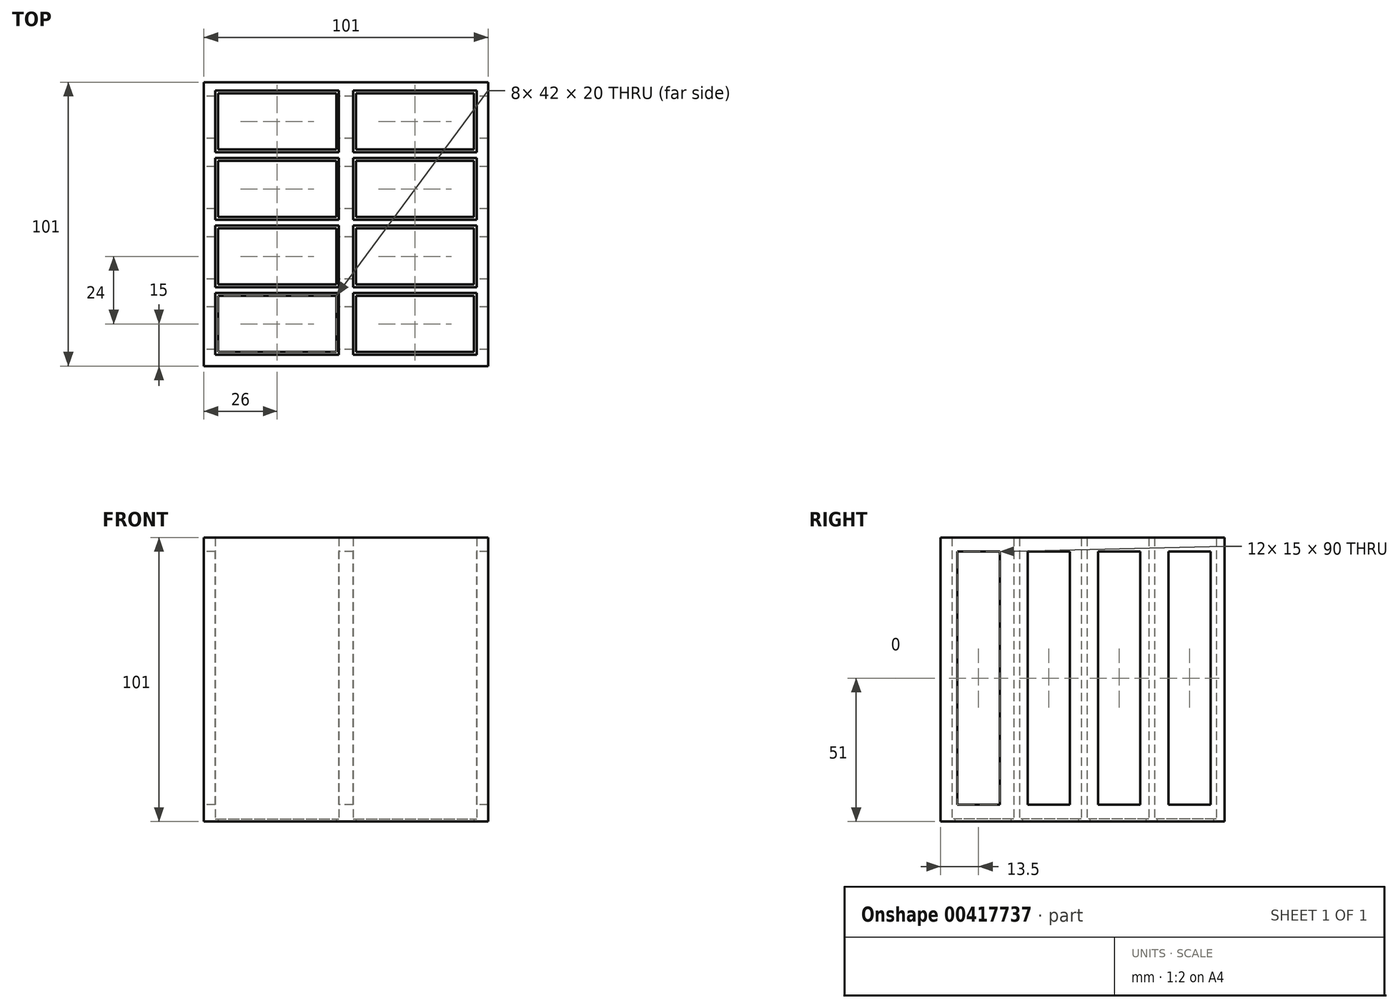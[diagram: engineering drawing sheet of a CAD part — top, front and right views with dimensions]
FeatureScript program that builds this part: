
annotation { "Feature Type Name" : "Feature", "Feature Type Description" : "" }
export const myFeature = defineFeature(function(context is Context, id is Id, definition is map)
    precondition{}
    {
        {
            var Q0;
            Q0=qCreatedBy(makeId("Top.planeOp"),FACE);
            var sketch = newSketch(context, id + "F0", { "sketchPlane" : qUnion([Q0])});
            skLineSegment(sketch, "E0.bottom", {"start": v(0, 0) * mm, "end": v(101, 0) * mm});
            skLineSegment(sketch, "E0.top", {"start": v(0, 101) * mm, "end": v(101, 101) * mm});
            skLineSegment(sketch, "E0.left", {"start": v(0, 0) * mm, "end": v(0, 101) * mm});
            skLineSegment(sketch, "E0.right", {"start": v(101, 0) * mm, "end": v(101, 101) * mm});
            skLineSegment(sketch, "E1.bottom", {"start": v(5, 97) * mm, "end": v(47, 97) * mm});
            skLineSegment(sketch, "E1.top", {"start": v(5, 77) * mm, "end": v(47, 77) * mm});
            skLineSegment(sketch, "E1.left", {"start": v(5, 97) * mm, "end": v(5, 77) * mm});
            skLineSegment(sketch, "E1.right", {"start": v(47, 97) * mm, "end": v(47, 77) * mm});
            skLineSegment(sketch, "E2.0.1.0", {"start": v(5, 73) * mm, "end": v(47, 73) * mm});
            skLineSegment(sketch, "E2.0.1.1", {"start": v(5, 73) * mm, "end": v(5, 53) * mm});
            skLineSegment(sketch, "E2.0.1.2", {"start": v(5, 53) * mm, "end": v(47, 53) * mm});
            skLineSegment(sketch, "E2.0.1.3", {"start": v(47, 73) * mm, "end": v(47, 53) * mm});
            skLineSegment(sketch, "E2.0.2.0", {"start": v(5, 49) * mm, "end": v(47, 49) * mm});
            skLineSegment(sketch, "E2.0.2.1", {"start": v(5, 49) * mm, "end": v(5, 29) * mm});
            skLineSegment(sketch, "E2.0.2.2", {"start": v(5, 29) * mm, "end": v(47, 29) * mm});
            skLineSegment(sketch, "E2.0.2.3", {"start": v(47, 49) * mm, "end": v(47, 29) * mm});
            skLineSegment(sketch, "E2.0.3.0", {"start": v(5, 25) * mm, "end": v(47, 25) * mm});
            skLineSegment(sketch, "E2.0.3.1", {"start": v(5, 25) * mm, "end": v(5, 5) * mm});
            skLineSegment(sketch, "E2.0.3.2", {"start": v(5, 5) * mm, "end": v(47, 5) * mm});
            skLineSegment(sketch, "E2.0.3.3", {"start": v(47, 25) * mm, "end": v(47, 5) * mm});
            skLineSegment(sketch, "E2.1.0.0", {"start": v(54, 97) * mm, "end": v(96, 97) * mm});
            skLineSegment(sketch, "E2.1.0.1", {"start": v(54, 97) * mm, "end": v(54, 77) * mm});
            skLineSegment(sketch, "E2.1.0.2", {"start": v(54, 77) * mm, "end": v(96, 77) * mm});
            skLineSegment(sketch, "E2.1.0.3", {"start": v(96, 97) * mm, "end": v(96, 77) * mm});
            skLineSegment(sketch, "E2.1.1.0", {"start": v(54, 73) * mm, "end": v(96, 73) * mm});
            skLineSegment(sketch, "E2.1.1.1", {"start": v(54, 73) * mm, "end": v(54, 53) * mm});
            skLineSegment(sketch, "E2.1.1.2", {"start": v(54, 53) * mm, "end": v(96, 53) * mm});
            skLineSegment(sketch, "E2.1.1.3", {"start": v(96, 73) * mm, "end": v(96, 53) * mm});
            skLineSegment(sketch, "E2.1.2.0", {"start": v(54, 49) * mm, "end": v(96, 49) * mm});
            skLineSegment(sketch, "E2.1.2.1", {"start": v(54, 49) * mm, "end": v(54, 29) * mm});
            skLineSegment(sketch, "E2.1.2.2", {"start": v(54, 29) * mm, "end": v(96, 29) * mm});
            skLineSegment(sketch, "E2.1.2.3", {"start": v(96, 49) * mm, "end": v(96, 29) * mm});
            skLineSegment(sketch, "E2.1.3.0", {"start": v(54, 25) * mm, "end": v(96, 25) * mm});
            skLineSegment(sketch, "E2.1.3.1", {"start": v(54, 25) * mm, "end": v(54, 5) * mm});
            skLineSegment(sketch, "E2.1.3.2", {"start": v(54, 5) * mm, "end": v(96, 5) * mm});
            skLineSegment(sketch, "E2.1.3.3", {"start": v(96, 25) * mm, "end": v(96, 5) * mm});
            skLineSegment(sketch, "E2.direction1", {"start": v(5, 97) * mm, "end": v(54, 97) * mm, "construction": true});
            skLineSegment(sketch, "E2.direction2", {"start": v(5, 97) * mm, "end": v(5, 73) * mm, "construction": true});
            skSolve(sketch);
        }
        {
            var Q0;
            Q0=makeQuery(id+"F0.imprint","IMPRINT",FACE,{"disambiguationData":[TD([[makeQuery(id+"F0.imprint","IMPRINT",EDGE,{"derivedFrom":sQuery(id+"F0.wireOp",EDGE,"E0.bottom")}),1.0]])]});
            extrude(context, id + "F1", {"entities" : qUnion([Q0]), "depth" : 1 * mm});
        }
        {
            var Q0;
            Q0=makeQuery(id+"F1.opExtrude","CAP_FACE",FACE,{"disambiguationData":[OSD([sQuery(id+"F0.wireOp",EDGE,"E0.bottom"),sQuery(id+"F0.wireOp",EDGE,"E0.top"),sQuery(id+"F0.wireOp",EDGE,"E0.left"),sQuery(id+"F0.wireOp",EDGE,"E0.right"),sQuery(id+"F0.wireOp",EDGE,"wlD0TPvz-95lD-sUnw-xDtB-dJjJsXXhuW11.bottom"),sQuery(id+"F0.wireOp",EDGE,"wlD0TPvz-95lD-sUnw-xDtB-dJjJsXXhuW11.top"),sQuery(id+"F0.wireOp",EDGE,"wlD0TPvz-95lD-sUnw-xDtB-dJjJsXXhuW11.left"),sQuery(id+"F0.wireOp",EDGE,"wlD0TPvz-95lD-sUnw-xDtB-dJjJsXXhuW11.right"),sQuery(id+"F0.wireOp",EDGE,"ddb73950-9b5f-4289-ac6a-2f79f204a4dd.0.1.0"),sQuery(id+"F0.wireOp",EDGE,"ddb73950-9b5f-4289-ac6a-2f79f204a4dd.0.1.1"),sQuery(id+"F0.wireOp",EDGE,"ddb73950-9b5f-4289-ac6a-2f79f204a4dd.0.1.2"),sQuery(id+"F0.wireOp",EDGE,"ddb73950-9b5f-4289-ac6a-2f79f204a4dd.0.1.3"),sQuery(id+"F0.wireOp",EDGE,"ddb73950-9b5f-4289-ac6a-2f79f204a4dd.1.0.0"),sQuery(id+"F0.wireOp",EDGE,"ddb73950-9b5f-4289-ac6a-2f79f204a4dd.1.0.1"),sQuery(id+"F0.wireOp",EDGE,"ddb73950-9b5f-4289-ac6a-2f79f204a4dd.1.0.2"),sQuery(id+"F0.wireOp",EDGE,"ddb73950-9b5f-4289-ac6a-2f79f204a4dd.1.0.3"),sQuery(id+"F0.wireOp",EDGE,"ddb73950-9b5f-4289-ac6a-2f79f204a4dd.1.1.0"),sQuery(id+"F0.wireOp",EDGE,"ddb73950-9b5f-4289-ac6a-2f79f204a4dd.1.1.1"),sQuery(id+"F0.wireOp",EDGE,"ddb73950-9b5f-4289-ac6a-2f79f204a4dd.1.1.2"),sQuery(id+"F0.wireOp",EDGE,"ddb73950-9b5f-4289-ac6a-2f79f204a4dd.1.1.3")])],"isStart":false});
            var sketch = newSketch(context, id + "F2", { "sketchPlane" : qUnion([Q0])});
            skLineSegment(sketch, "E3.0.0", {"start": v(101, 101) * mm, "end": v(0, 101) * mm});
            skLineSegment(sketch, "E3.0.1", {"start": v(0, 101) * mm, "end": v(0, 0) * mm});
            skLineSegment(sketch, "E3.0.2", {"start": v(0, 0) * mm, "end": v(101, 0) * mm});
            skLineSegment(sketch, "E3.0.3", {"start": v(101, 0) * mm, "end": v(101, 101) * mm});
            skLineSegment(sketch, "E4.0", {"start": v(4, 98) * mm, "end": v(48, 98) * mm});
            skLineSegment(sketch, "E4.1", {"start": v(4, 98) * mm, "end": v(4, 76) * mm});
            skLineSegment(sketch, "E4.2", {"start": v(4, 76) * mm, "end": v(48, 76) * mm});
            skLineSegment(sketch, "E4.3", {"start": v(48, 98) * mm, "end": v(48, 76) * mm});
            skLineSegment(sketch, "E5.0.1.0", {"start": v(48, 74) * mm, "end": v(48, 52) * mm});
            skLineSegment(sketch, "E5.0.1.1", {"start": v(4, 74) * mm, "end": v(48, 74) * mm});
            skLineSegment(sketch, "E5.0.1.2", {"start": v(4, 74) * mm, "end": v(4, 52) * mm});
            skLineSegment(sketch, "E5.0.1.3", {"start": v(4, 52) * mm, "end": v(48, 52) * mm});
            skLineSegment(sketch, "E5.0.2.0", {"start": v(48, 50) * mm, "end": v(48, 28) * mm});
            skLineSegment(sketch, "E5.0.2.1", {"start": v(4, 50) * mm, "end": v(48, 50) * mm});
            skLineSegment(sketch, "E5.0.2.2", {"start": v(4, 50) * mm, "end": v(4, 28) * mm});
            skLineSegment(sketch, "E5.0.2.3", {"start": v(4, 28) * mm, "end": v(48, 28) * mm});
            skLineSegment(sketch, "E5.0.3.0", {"start": v(48, 26) * mm, "end": v(48, 4) * mm});
            skLineSegment(sketch, "E5.0.3.1", {"start": v(4, 26) * mm, "end": v(48, 26) * mm});
            skLineSegment(sketch, "E5.0.3.2", {"start": v(4, 26) * mm, "end": v(4, 4) * mm});
            skLineSegment(sketch, "E5.0.3.3", {"start": v(4, 4) * mm, "end": v(48, 4) * mm});
            skLineSegment(sketch, "E5.1.0.0", {"start": v(97, 98) * mm, "end": v(97, 76) * mm});
            skLineSegment(sketch, "E5.1.0.1", {"start": v(53, 98) * mm, "end": v(97, 98) * mm});
            skLineSegment(sketch, "E5.1.0.2", {"start": v(53, 98) * mm, "end": v(53, 76) * mm});
            skLineSegment(sketch, "E5.1.0.3", {"start": v(53, 76) * mm, "end": v(97, 76) * mm});
            skLineSegment(sketch, "E5.1.1.0", {"start": v(97, 74) * mm, "end": v(97, 52) * mm});
            skLineSegment(sketch, "E5.1.1.1", {"start": v(53, 74) * mm, "end": v(97, 74) * mm});
            skLineSegment(sketch, "E5.1.1.2", {"start": v(53, 74) * mm, "end": v(53, 52) * mm});
            skLineSegment(sketch, "E5.1.1.3", {"start": v(53, 52) * mm, "end": v(97, 52) * mm});
            skLineSegment(sketch, "E5.1.2.0", {"start": v(97, 50) * mm, "end": v(97, 28) * mm});
            skLineSegment(sketch, "E5.1.2.1", {"start": v(53, 50) * mm, "end": v(97, 50) * mm});
            skLineSegment(sketch, "E5.1.2.2", {"start": v(53, 50) * mm, "end": v(53, 28) * mm});
            skLineSegment(sketch, "E5.1.2.3", {"start": v(53, 28) * mm, "end": v(97, 28) * mm});
            skLineSegment(sketch, "E5.1.3.0", {"start": v(97, 26) * mm, "end": v(97, 4) * mm});
            skLineSegment(sketch, "E5.1.3.1", {"start": v(53, 26) * mm, "end": v(97, 26) * mm});
            skLineSegment(sketch, "E5.1.3.2", {"start": v(53, 26) * mm, "end": v(53, 4) * mm});
            skLineSegment(sketch, "E5.1.3.3", {"start": v(53, 4) * mm, "end": v(97, 4) * mm});
            skLineSegment(sketch, "E5.direction1", {"start": v(49, 75) * mm, "end": v(98, 75) * mm, "construction": true});
            skLineSegment(sketch, "E5.direction2", {"start": v(49, 75) * mm, "end": v(49, 51) * mm, "construction": true});
            skSolve(sketch);
        }
        {
            var Q0;
            Q0 = qSketchRegion(id + "F2", true);
            extrude(context, id + "F3", {"entities" : qUnion([Q0]), "operationType" : NewBodyOperationType.ADD, "depth" : 100 * mm});
        }
        {
            var Q0;
            Q0=makeQuery(id+"F3.boolean.opBoolean","MERGE",FACE,{"derivedFrom":[makeQuery(id+"F1.opExtrude","SWEPT_FACE",FACE,{"disambiguationData":[OSD([sQuery(id+"F0.wireOp",EDGE,"E0.left")])]}),makeQuery(id+"F3.opExtrude","SWEPT_FACE",FACE,{"disambiguationData":[OSD([sQuery(id+"F2.wireOp",EDGE,"a62dd570-20e1-4e47-a6b2-986de0098e9a.0.1")])]})]});
            var sketch = newSketch(context, id + "F4", { "sketchPlane" : qUnion([Q0])});
            skLineSegment(sketch, "E6.0.0", {"start": v(-101, 0) * mm, "end": v(0, 0) * mm, "construction": true});
            skLineSegment(sketch, "E6.0.1", {"start": v(0, 0) * mm, "end": v(0, 101) * mm, "construction": true});
            skLineSegment(sketch, "E6.0.2", {"start": v(0, 101) * mm, "end": v(-101, 101) * mm, "construction": true});
            skLineSegment(sketch, "E6.0.3", {"start": v(-101, 101) * mm, "end": v(-101, 0) * mm, "construction": true});
            skLineSegment(sketch, "E7.bottom", {"start": v(-96, 96) * mm, "end": v(-81, 96) * mm});
            skLineSegment(sketch, "E7.top", {"start": v(-96, 6) * mm, "end": v(-81, 6) * mm});
            skLineSegment(sketch, "E7.left", {"start": v(-96, 96) * mm, "end": v(-96, 6) * mm});
            skLineSegment(sketch, "E7.right", {"start": v(-81, 96) * mm, "end": v(-81, 6) * mm});
            skLineSegment(sketch, "E8.1.0.0", {"start": v(-56, 96) * mm, "end": v(-56, 6) * mm});
            skLineSegment(sketch, "E8.1.0.1", {"start": v(-71, 96) * mm, "end": v(-56, 96) * mm});
            skLineSegment(sketch, "E8.1.0.2", {"start": v(-71, 96) * mm, "end": v(-71, 6) * mm});
            skLineSegment(sketch, "E8.1.0.3", {"start": v(-71, 6) * mm, "end": v(-56, 6) * mm});
            skLineSegment(sketch, "E8.2.0.0", {"start": v(-31, 96) * mm, "end": v(-31, 6) * mm});
            skLineSegment(sketch, "E8.2.0.1", {"start": v(-46, 96) * mm, "end": v(-31, 96) * mm});
            skLineSegment(sketch, "E8.2.0.2", {"start": v(-46, 96) * mm, "end": v(-46, 6) * mm});
            skLineSegment(sketch, "E8.2.0.3", {"start": v(-46, 6) * mm, "end": v(-31, 6) * mm});
            skLineSegment(sketch, "E8.3.0.0", {"start": v(-6, 96) * mm, "end": v(-6, 6) * mm});
            skLineSegment(sketch, "E8.3.0.1", {"start": v(-21, 96) * mm, "end": v(-6, 96) * mm});
            skLineSegment(sketch, "E8.3.0.2", {"start": v(-21, 96) * mm, "end": v(-21, 6) * mm});
            skLineSegment(sketch, "E8.3.0.3", {"start": v(-21, 6) * mm, "end": v(-6, 6) * mm});
            skLineSegment(sketch, "E8.direction1", {"start": v(-81, 6) * mm, "end": v(-56, 6) * mm, "construction": true});
            skSolve(sketch);
        }
        {
            var Q0;
            Q0 = qSketchRegion(id + "F4", true);
            extrude(context, id + "F5", {"entities" : qUnion([Q0]), "operationType" : NewBodyOperationType.REMOVE, "endBound" : BoundingType.THROUGH_ALL, "oppositeDirection" : true, "depth" : 25 * mm});
        }
    });
